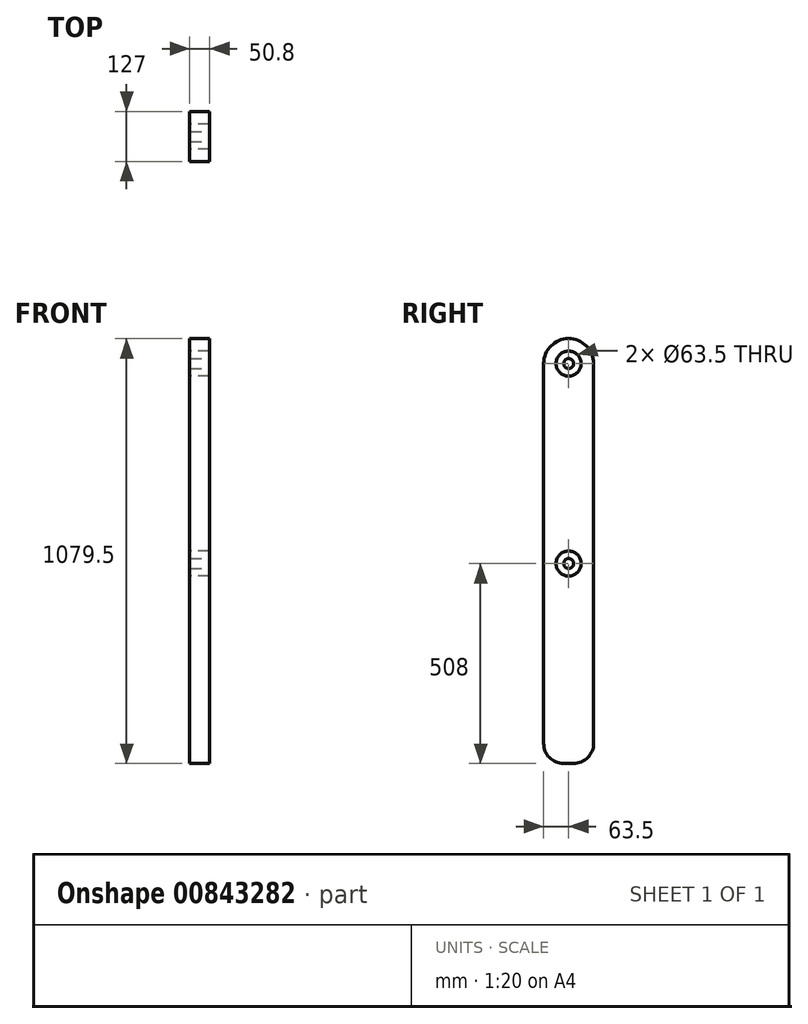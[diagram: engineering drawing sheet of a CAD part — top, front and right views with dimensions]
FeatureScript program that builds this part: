
annotation { "Feature Type Name" : "Feature", "Feature Type Description" : "" }
export const myFeature = defineFeature(function(context is Context, id is Id, definition is map)
    precondition{}
    {
        {
            var Q0;
            Q0=qCreatedBy(makeId("Right.planeOp"),FACE);
            var sketch = newSketch(context, id + "F0", { "sketchPlane" : qUnion([Q0])});
            skLineSegment(sketch, "E0.bottom", {"start": v(50.8, 0) * mm, "end": v(76.2, 0) * mm});
            skLineSegment(sketch, "E0.left", {"start": v(0, 50.8) * mm, "end": v(0, 1016) * mm});
            skLineSegment(sketch, "E0.right", {"start": v(127, 50.8) * mm, "end": v(127, 1016) * mm});
            skArc(sketch, "E1", {"start": v(127, 1016) * mm, "mid": v(63.5, 1079.5) * mm, "end": v(0, 1016) * mm});
            skCircle(sketch, "E2", {"center": v(63.5, 1016) * mm, "radius": 31.75 * mm});
            skPoint(sketch, "E3.visualSharp", {"position": v(127, 0) * mm});
            skArc(sketch, "E3.filletArc", {"start": v(76.2, 0) * mm, "mid": v(112.12, 14.88) * mm, "end": v(127, 50.8) * mm});
            skPoint(sketch, "E4.visualSharp", {"position": v(0, 0) * mm});
            skArc(sketch, "E4.filletArc", {"start": v(0, 50.8) * mm, "mid": v(14.88, 14.88) * mm, "end": v(50.8, 0) * mm});
            skCircle(sketch, "E5", {"center": v(63.5, 508) * mm, "radius": 31.75 * mm});
            skSolve(sketch);
        }
        {
            var Q0;
            Q0=makeQuery(id+"F0.imprint","IMPRINT",FACE,{"disambiguationData":[TD([[makeQuery(id+"F0.imprint","IMPRINT",EDGE,{"derivedFrom":sQuery(id+"F0.wireOp",EDGE,"E0.bottom")}),1.0]])]});
            extrude(context, id + "F1", {"entities" : qUnion([Q0]), "depth" : 50.8 * mm, "offsetDistance" : 25.4 * mm});
        }
        {
            var Q0;
            Q0=makeQuery(id+"F1.opExtrude","CAP_FACE",FACE,{"disambiguationData":[OSD([sQuery(id+"F0.wireOp",EDGE,"E0.bottom"),sQuery(id+"F0.wireOp",EDGE,"E0.left"),sQuery(id+"F0.wireOp",EDGE,"E0.right"),sQuery(id+"F0.wireOp",EDGE,"E1"),sQuery(id+"F0.wireOp",EDGE,"E2"),sQuery(id+"F0.wireOp",EDGE,"E3.filletArc"),sQuery(id+"F0.wireOp",EDGE,"E4.filletArc"),sQuery(id+"F0.wireOp",EDGE,"E5")])],"isStart":false});
            var sketch = newSketch(context, id + "F2", { "sketchPlane" : qUnion([Q0])});
            skCircle(sketch, "E6", {"center": v(63.5, 1016) * mm, "radius": 12.7 * mm});
            skCircle(sketch, "E7", {"center": v(63.5, 508) * mm, "radius": 12.7 * mm});
            skSolve(sketch);
        }
        {
            var Q0;
            Q0 = qSketchRegion(id + "F2", true);
            extrude(context, id + "F3", {"entities" : qUnion([Q0]), "oppositeDirection" : true, "depth" : 50.8 * mm, "offsetDistance" : 25.4 * mm});
        }
    });
